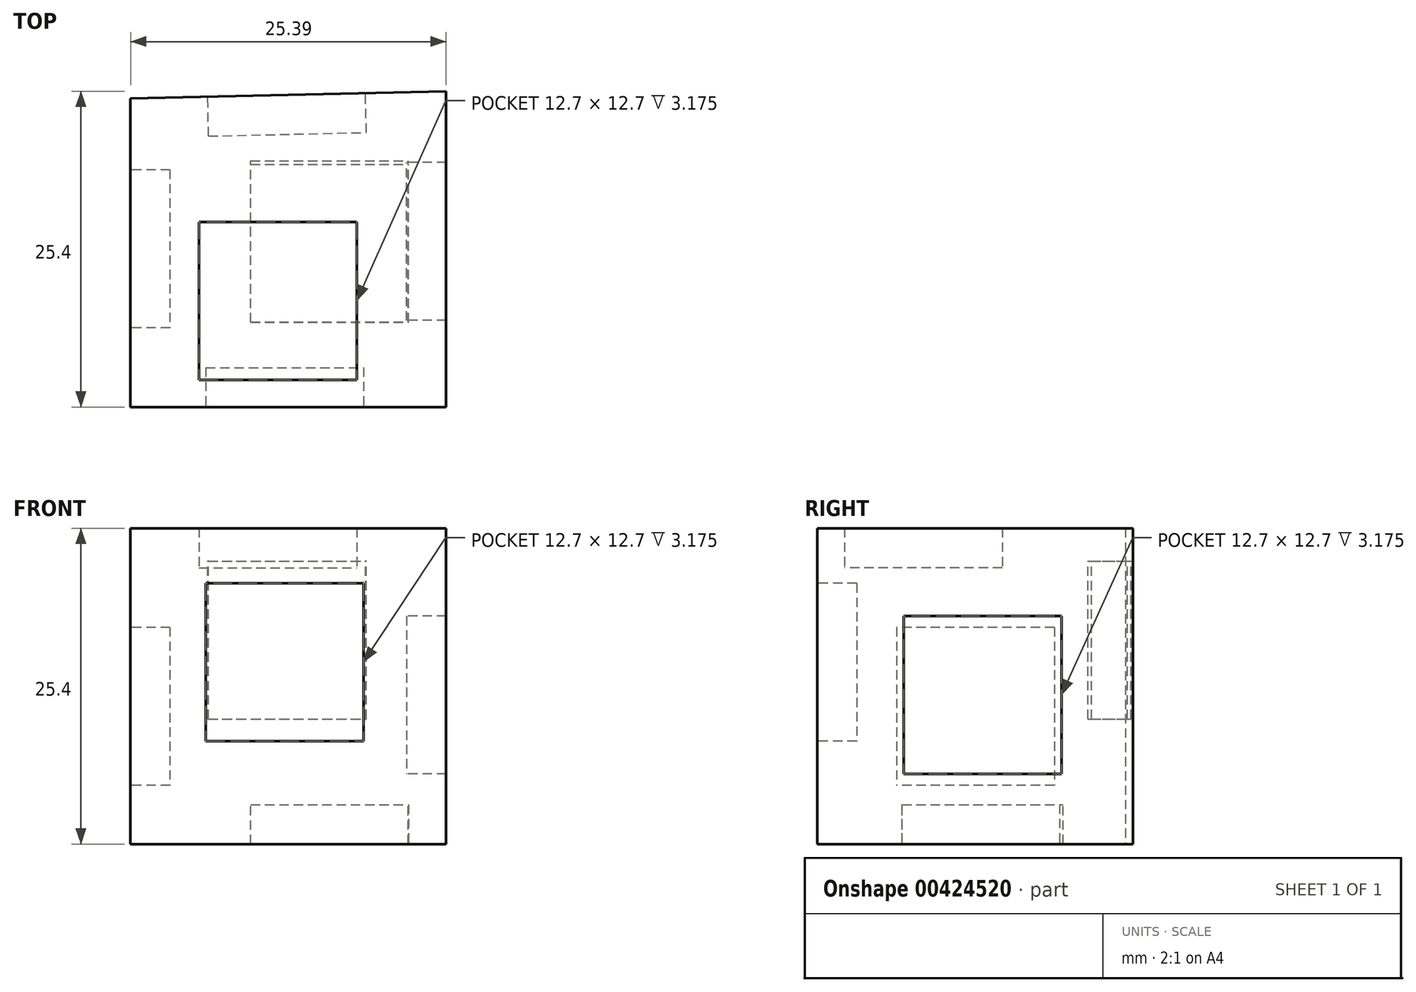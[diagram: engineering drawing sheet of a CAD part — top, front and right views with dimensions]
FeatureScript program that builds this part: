
annotation { "Feature Type Name" : "Feature", "Feature Type Description" : "" }
export const myFeature = defineFeature(function(context is Context, id is Id, definition is map)
    precondition{}
    {
        {
            var Q0;
            Q0=qCreatedBy(makeId("Top.planeOp"),FACE);
            var sketch = newSketch(context, id + "F0", { "sketchPlane" : qUnion([Q0])});
            skLineSegment(sketch, "E0", {"start": v(-9.67, 9.92) * mm, "end": v(-9.67, -14.9) * mm});
            skLineSegment(sketch, "E1", {"start": v(-9.67, -14.9) * mm, "end": v(15.72, -14.9) * mm});
            skLineSegment(sketch, "E2", {"start": v(15.72, -14.9) * mm, "end": v(15.72, 10.5) * mm});
            skLineSegment(sketch, "E3", {"start": v(-9.67, 9.92) * mm, "end": v(15.72, 10.5) * mm});
            skSolve(sketch);
        }
        {
            var Q0;
            Q0 = qSketchRegion(id + "F0", true);
            extrude(context, id + "F1", {"entities" : qUnion([Q0]), "depth" : 25.4 * mm});
        }
        {
            var Q0;
            Q0=makeQuery(id+"F1.opExtrude","CAP_FACE",FACE,{"disambiguationData":[OSD([sQuery(id+"F0.wireOp",EDGE,"E0"),sQuery(id+"F0.wireOp",EDGE,"E1"),sQuery(id+"F0.wireOp",EDGE,"E2"),sQuery(id+"F0.wireOp",EDGE,"E3")])],"isStart":false});
            var sketch = newSketch(context, id + "F2", { "sketchPlane" : qUnion([Q0])});
            skLineSegment(sketch, "E4.bottom", {"start": v(-4.16, 0) * mm, "end": v(8.54, 0) * mm});
            skLineSegment(sketch, "E4.top", {"start": v(-4.16, -12.7) * mm, "end": v(8.54, -12.7) * mm});
            skLineSegment(sketch, "E4.left", {"start": v(-4.16, 0) * mm, "end": v(-4.16, -12.7) * mm});
            skLineSegment(sketch, "E4.right", {"start": v(8.54, 0) * mm, "end": v(8.54, -12.7) * mm});
            skSolve(sketch);
        }
        {
            var Q0;
            Q0=makeQuery(id+"F2.imprint","IMPRINT",FACE,{"disambiguationData":[TD([[makeQuery(id+"F2.imprint","IMPRINT",EDGE,{"derivedFrom":sQuery(id+"F2.wireOp",EDGE,"E4.bottom")}),-1.0]])]});
            extrude(context, id + "F3", {"entities" : qUnion([Q0]), "operationType" : NewBodyOperationType.REMOVE, "oppositeDirection" : true, "depth" : 3.17 * mm});
        }
        {
            var Q0;
            Q0=makeQuery(id+"F1.opExtrude","SWEPT_FACE",FACE,{"disambiguationData":[OSD([sQuery(id+"F0.wireOp",EDGE,"E2")])]});
            var sketch = newSketch(context, id + "F4", { "sketchPlane" : qUnion([Q0])});
            skLineSegment(sketch, "E5.bottom", {"start": v(-7.93, 18.33) * mm, "end": v(4.77, 18.33) * mm});
            skLineSegment(sketch, "E5.top", {"start": v(-7.93, 5.63) * mm, "end": v(4.77, 5.63) * mm});
            skLineSegment(sketch, "E5.left", {"start": v(-7.93, 18.33) * mm, "end": v(-7.93, 5.63) * mm});
            skLineSegment(sketch, "E5.right", {"start": v(4.77, 18.33) * mm, "end": v(4.77, 5.63) * mm});
            skSolve(sketch);
        }
        {
            var Q0;
            Q0=makeQuery(id+"F4.imprint","IMPRINT",FACE,{"disambiguationData":[TD([[makeQuery(id+"F4.imprint","IMPRINT",EDGE,{"derivedFrom":sQuery(id+"F4.wireOp",EDGE,"E5.bottom")}),-1.0]])]});
            extrude(context, id + "F5", {"entities" : qUnion([Q0]), "operationType" : NewBodyOperationType.REMOVE, "oppositeDirection" : true, "depth" : 3.17 * mm});
        }
        {
            var Q0;
            Q0=makeQuery(id+"F1.opExtrude","SWEPT_FACE",FACE,{"disambiguationData":[OSD([sQuery(id+"F0.wireOp",EDGE,"E1")])]});
            var sketch = newSketch(context, id + "F6", { "sketchPlane" : qUnion([Q0])});
            skLineSegment(sketch, "E6.bottom", {"start": v(-3.62, 20.96) * mm, "end": v(9.08, 20.96) * mm});
            skLineSegment(sketch, "E6.top", {"start": v(-3.62, 8.26) * mm, "end": v(9.08, 8.26) * mm});
            skLineSegment(sketch, "E6.left", {"start": v(-3.62, 20.96) * mm, "end": v(-3.62, 8.26) * mm});
            skLineSegment(sketch, "E6.right", {"start": v(9.08, 20.96) * mm, "end": v(9.08, 8.26) * mm});
            skSolve(sketch);
        }
        {
            var Q0;
            Q0=makeQuery(id+"F6.imprint","IMPRINT",FACE,{"disambiguationData":[TD([[makeQuery(id+"F6.imprint","IMPRINT",EDGE,{"derivedFrom":sQuery(id+"F6.wireOp",EDGE,"E6.bottom")}),-1.0]])]});
            extrude(context, id + "F7", {"entities" : qUnion([Q0]), "operationType" : NewBodyOperationType.REMOVE, "oppositeDirection" : true, "depth" : 3.17 * mm});
        }
        {
            var Q0;
            Q0=makeQuery(id+"F1.opExtrude","CAP_FACE",FACE,{"disambiguationData":[OSD([sQuery(id+"F0.wireOp",EDGE,"E0"),sQuery(id+"F0.wireOp",EDGE,"E1"),sQuery(id+"F0.wireOp",EDGE,"E2"),sQuery(id+"F0.wireOp",EDGE,"E3")])],"isStart":true});
            var sketch = newSketch(context, id + "F8", { "sketchPlane" : qUnion([Q0])});
            skLineSegment(sketch, "E7.bottom", {"start": v(0, 8.08) * mm, "end": v(12.7, 8.08) * mm});
            skLineSegment(sketch, "E7.top", {"start": v(0, -4.62) * mm, "end": v(12.7, -4.62) * mm});
            skLineSegment(sketch, "E7.left", {"start": v(0, 8.08) * mm, "end": v(0, -4.62) * mm});
            skLineSegment(sketch, "E7.right", {"start": v(12.7, 8.08) * mm, "end": v(12.7, -4.62) * mm});
            skSolve(sketch);
        }
        {
            var Q0;
            Q0 = qSketchRegion(id + "F8", true);
            extrude(context, id + "F9", {"entities" : qUnion([Q0]), "operationType" : NewBodyOperationType.REMOVE, "oppositeDirection" : true, "depth" : 3.17 * mm});
        }
        {
            var Q0;
            Q0=makeQuery(id+"F1.opExtrude","SWEPT_FACE",FACE,{"disambiguationData":[OSD([sQuery(id+"F0.wireOp",EDGE,"E3")])]});
            var sketch = newSketch(context, id + "F10", { "sketchPlane" : qUnion([Q0])});
            skLineSegment(sketch, "E8.bottom", {"start": v(3.24, 10.06) * mm, "end": v(-9.46, 10.06) * mm});
            skLineSegment(sketch, "E8.top", {"start": v(3.24, 22.76) * mm, "end": v(-9.46, 22.76) * mm});
            skLineSegment(sketch, "E8.left", {"start": v(3.24, 10.06) * mm, "end": v(3.24, 22.76) * mm});
            skLineSegment(sketch, "E8.right", {"start": v(-9.46, 10.06) * mm, "end": v(-9.46, 22.76) * mm});
            skSolve(sketch);
        }
        {
            var Q0;
            Q0=makeQuery(id+"F10.imprint","IMPRINT",FACE,{"disambiguationData":[TD([[makeQuery(id+"F10.imprint","IMPRINT",EDGE,{"derivedFrom":sQuery(id+"F10.wireOp",EDGE,"E8.bottom")}),-1.0]])]});
            extrude(context, id + "F11", {"entities" : qUnion([Q0]), "operationType" : NewBodyOperationType.REMOVE, "oppositeDirection" : true, "depth" : 3.17 * mm});
        }
        {
            var Q0;
            Q0=makeQuery(id+"F1.opExtrude","SWEPT_FACE",FACE,{"disambiguationData":[OSD([sQuery(id+"F0.wireOp",EDGE,"E0")])]});
            var sketch = newSketch(context, id + "F12", { "sketchPlane" : qUnion([Q0])});
            skLineSegment(sketch, "E9.bottom", {"start": v(-4.2, 17.43) * mm, "end": v(8.5, 17.43) * mm});
            skLineSegment(sketch, "E9.top", {"start": v(-4.2, 4.73) * mm, "end": v(8.5, 4.73) * mm});
            skLineSegment(sketch, "E9.left", {"start": v(-4.2, 17.43) * mm, "end": v(-4.2, 4.73) * mm});
            skLineSegment(sketch, "E9.right", {"start": v(8.5, 17.43) * mm, "end": v(8.5, 4.73) * mm});
            skSolve(sketch);
        }
        {
            var Q0;
            Q0=makeQuery(id+"F12.imprint","IMPRINT",FACE,{"disambiguationData":[TD([[makeQuery(id+"F12.imprint","IMPRINT",EDGE,{"derivedFrom":sQuery(id+"F12.wireOp",EDGE,"E9.bottom")}),-1.0]])]});
            extrude(context, id + "F13", {"entities" : qUnion([Q0]), "operationType" : NewBodyOperationType.REMOVE, "oppositeDirection" : true, "depth" : 3.17 * mm});
        }
        {
            var Q0;
            Q0=makeQuery(id+"F3.boolean.opBoolean","COPY",FACE,{"derivedFrom":makeQuery(id+"F3.opExtrude","CAP_FACE",FACE,{"disambiguationData":[OSD([sQuery(id+"F2.wireOp",EDGE,"E4.bottom"),sQuery(id+"F2.wireOp",EDGE,"E4.top"),sQuery(id+"F2.wireOp",EDGE,"E4.left"),sQuery(id+"F2.wireOp",EDGE,"E4.right")])],"isStart":false})});
            var sketch = newSketch(context, id + "F14", { "sketchPlane" : qUnion([Q0])});
            skLineSegment(sketch, "E10.bottom", {"start": v(-4.16, 0) * mm, "end": v(8.54, 0) * mm});
            skLineSegment(sketch, "E10.top", {"start": v(-4.16, -12.7) * mm, "end": v(8.54, -12.7) * mm});
            skLineSegment(sketch, "E10.left", {"start": v(-4.16, 0) * mm, "end": v(-4.16, -12.7) * mm});
            skLineSegment(sketch, "E10.right", {"start": v(8.54, 0) * mm, "end": v(8.54, -12.7) * mm});
            skSolve(sketch);
        }
        {
            var Q0;
            Q0=makeQuery(id+"F14.imprint","IMPRINT",FACE,{"disambiguationData":[TD([[makeQuery(id+"F14.imprint","IMPRINT",EDGE,{"derivedFrom":sQuery(id+"F14.wireOp",EDGE,"E10.bottom")}),-1.0]])]});
            extrude(context, id + "F15", {"entities" : qUnion([Q0]), "depth" : 3.17 * mm});
        }
        {
            var Q0;
            Q0=makeQuery(id+"F5.boolean.opBoolean","COPY",FACE,{"derivedFrom":makeQuery(id+"F5.opExtrude","CAP_FACE",FACE,{"disambiguationData":[OSD([sQuery(id+"F4.wireOp",EDGE,"E5.bottom"),sQuery(id+"F4.wireOp",EDGE,"E5.top"),sQuery(id+"F4.wireOp",EDGE,"E5.left"),sQuery(id+"F4.wireOp",EDGE,"E5.right")])],"isStart":false})});
            var sketch = newSketch(context, id + "F16", { "sketchPlane" : qUnion([Q0])});
            skLineSegment(sketch, "E11.bottom", {"start": v(-7.93, 18.33) * mm, "end": v(4.77, 18.33) * mm});
            skLineSegment(sketch, "E11.top", {"start": v(-7.93, 5.63) * mm, "end": v(4.77, 5.63) * mm});
            skLineSegment(sketch, "E11.left", {"start": v(-7.93, 18.33) * mm, "end": v(-7.93, 5.63) * mm});
            skLineSegment(sketch, "E11.right", {"start": v(4.77, 18.33) * mm, "end": v(4.77, 5.63) * mm});
            skSolve(sketch);
        }
        {
            var Q0;
            Q0=makeQuery(id+"F16.imprint","IMPRINT",FACE,{"disambiguationData":[TD([[makeQuery(id+"F16.imprint","IMPRINT",EDGE,{"derivedFrom":sQuery(id+"F16.wireOp",EDGE,"E11.bottom")}),-1.0]])]});
            var sketch = newSketch(context, id + "F17", { "sketchPlane" : qUnion([Q0])});
            skSolve(sketch);
        }
        {
            var Q0;
            Q0 = qSketchRegion(id + "F17", true);
            var Q1;
            Q1=makeQuery(id+"F16.imprint","IMPRINT",FACE,{"disambiguationData":[TD([[makeQuery(id+"F16.imprint","IMPRINT",EDGE,{"derivedFrom":sQuery(id+"F16.wireOp",EDGE,"E11.bottom")}),-1.0]])]});
            extrude(context, id + "F18", {"entities" : qUnion([Q0, Q1]), "depth" : 3.17 * mm});
        }
        {
            var Q0;
            Q0=makeQuery(id+"F11.boolean.opBoolean","COPY",FACE,{"derivedFrom":makeQuery(id+"F11.opExtrude","CAP_FACE",FACE,{"disambiguationData":[OSD([sQuery(id+"F10.wireOp",EDGE,"E8.bottom"),sQuery(id+"F10.wireOp",EDGE,"E8.top"),sQuery(id+"F10.wireOp",EDGE,"E8.left"),sQuery(id+"F10.wireOp",EDGE,"E8.right")])],"isStart":false})});
            var sketch = newSketch(context, id + "F19", { "sketchPlane" : qUnion([Q0])});
            skLineSegment(sketch, "E12.bottom", {"start": v(-9.46, 22.76) * mm, "end": v(3.24, 22.76) * mm});
            skLineSegment(sketch, "E12.top", {"start": v(-9.46, 10.06) * mm, "end": v(3.24, 10.06) * mm});
            skLineSegment(sketch, "E12.left", {"start": v(-9.46, 22.76) * mm, "end": v(-9.46, 10.06) * mm});
            skLineSegment(sketch, "E12.right", {"start": v(3.24, 22.76) * mm, "end": v(3.24, 10.06) * mm});
            skSolve(sketch);
        }
        {
            var Q0;
            Q0=makeQuery(id+"F19.imprint","IMPRINT",FACE,{"disambiguationData":[TD([[makeQuery(id+"F19.imprint","IMPRINT",EDGE,{"derivedFrom":sQuery(id+"F19.wireOp",EDGE,"E12.bottom")}),1.0]])]});
            var sketch = newSketch(context, id + "F20", { "sketchPlane" : qUnion([Q0])});
            skSolve(sketch);
        }
        {
            var Q0;
            Q0 = qSketchRegion(id + "F20", true);
            var Q1;
            Q1=makeQuery(id+"F19.imprint","IMPRINT",FACE,{"disambiguationData":[TD([[makeQuery(id+"F19.imprint","IMPRINT",EDGE,{"derivedFrom":sQuery(id+"F19.wireOp",EDGE,"E12.bottom")}),1.0]])]});
            extrude(context, id + "F21", {"entities" : qUnion([Q0, Q1]), "depth" : 3.17 * mm});
        }
        {
            var Q0;
            Q0=makeQuery(id+"F13.boolean.opBoolean","COPY",FACE,{"derivedFrom":makeQuery(id+"F13.opExtrude","CAP_FACE",FACE,{"disambiguationData":[OSD([sQuery(id+"F12.wireOp",EDGE,"E9.bottom"),sQuery(id+"F12.wireOp",EDGE,"E9.top"),sQuery(id+"F12.wireOp",EDGE,"E9.left"),sQuery(id+"F12.wireOp",EDGE,"E9.right")])],"isStart":false})});
            var sketch = newSketch(context, id + "F22", { "sketchPlane" : qUnion([Q0])});
            skLineSegment(sketch, "E13.bottom", {"start": v(-4.2, 17.43) * mm, "end": v(8.5, 17.43) * mm});
            skLineSegment(sketch, "E13.top", {"start": v(-4.2, 4.73) * mm, "end": v(8.5, 4.73) * mm});
            skLineSegment(sketch, "E13.left", {"start": v(-4.2, 17.43) * mm, "end": v(-4.2, 4.73) * mm});
            skLineSegment(sketch, "E13.right", {"start": v(8.5, 17.43) * mm, "end": v(8.5, 4.73) * mm});
            skSolve(sketch);
        }
        {
            var Q0;
            Q0 = qSketchRegion(id + "F22", true);
            extrude(context, id + "F23", {"entities" : qUnion([Q0]), "depth" : 3.17 * mm});
        }
        {
            var Q0;
            Q0=makeQuery(id+"F7.boolean.opBoolean","COPY",FACE,{"derivedFrom":makeQuery(id+"F7.opExtrude","CAP_FACE",FACE,{"disambiguationData":[OSD([sQuery(id+"F6.wireOp",EDGE,"E6.bottom"),sQuery(id+"F6.wireOp",EDGE,"E6.top"),sQuery(id+"F6.wireOp",EDGE,"E6.left"),sQuery(id+"F6.wireOp",EDGE,"E6.right")])],"isStart":false})});
            var sketch = newSketch(context, id + "F24", { "sketchPlane" : qUnion([Q0])});
            skLineSegment(sketch, "E14.bottom", {"start": v(-3.62, 20.96) * mm, "end": v(9.08, 20.96) * mm});
            skLineSegment(sketch, "E14.top", {"start": v(-3.62, 8.26) * mm, "end": v(9.08, 8.26) * mm});
            skLineSegment(sketch, "E14.left", {"start": v(-3.62, 20.96) * mm, "end": v(-3.62, 8.26) * mm});
            skLineSegment(sketch, "E14.right", {"start": v(9.08, 20.96) * mm, "end": v(9.08, 8.26) * mm});
            skSolve(sketch);
        }
        {
            var Q0;
            Q0 = qSketchRegion(id + "F24", true);
            extrude(context, id + "F25", {"entities" : qUnion([Q0]), "depth" : 3.17 * mm});
        }
        {
            var Q0;
            Q0=makeQuery(id+"F9.boolean.opBoolean","COPY",FACE,{"derivedFrom":makeQuery(id+"F9.opExtrude","CAP_FACE",FACE,{"disambiguationData":[OSD([sQuery(id+"F8.wireOp",EDGE,"E7.bottom"),sQuery(id+"F8.wireOp",EDGE,"E7.top"),sQuery(id+"F8.wireOp",EDGE,"E7.left"),sQuery(id+"F8.wireOp",EDGE,"E7.right")])],"isStart":false})});
            var sketch = newSketch(context, id + "F26", { "sketchPlane" : qUnion([Q0])});
            skLineSegment(sketch, "E15.bottom", {"start": v(0, 8.08) * mm, "end": v(12.7, 8.08) * mm});
            skLineSegment(sketch, "E15.top", {"start": v(0, -4.62) * mm, "end": v(12.7, -4.62) * mm});
            skLineSegment(sketch, "E15.left", {"start": v(0, 8.08) * mm, "end": v(0, -4.62) * mm});
            skLineSegment(sketch, "E15.right", {"start": v(12.7, 8.08) * mm, "end": v(12.7, -4.62) * mm});
            skSolve(sketch);
        }
        {
            var Q0;
            Q0=makeQuery(id+"F26.imprint","IMPRINT",FACE,{"disambiguationData":[TD([[makeQuery(id+"F26.imprint","IMPRINT",EDGE,{"derivedFrom":sQuery(id+"F26.wireOp",EDGE,"E15.bottom")}),-1.0]])]});
            var sketch = newSketch(context, id + "F27", { "sketchPlane" : qUnion([Q0])});
            skLineSegment(sketch, "E16.bottom", {"start": v(0, 8.06) * mm, "end": v(12.66, 8.06) * mm});
            skLineSegment(sketch, "E16.top", {"start": v(0, -4.9) * mm, "end": v(12.66, -4.9) * mm});
            skLineSegment(sketch, "E16.left", {"start": v(0, 8.06) * mm, "end": v(0, -4.9) * mm});
            skLineSegment(sketch, "E16.right", {"start": v(12.66, 8.06) * mm, "end": v(12.66, -4.9) * mm});
            skSolve(sketch);
        }
        {
            var Q0;
            Q0 = qSketchRegion(id + "F27", true);
            extrude(context, id + "F28", {"entities" : qUnion([Q0]), "depth" : 3.17 * mm});
        }
    });
